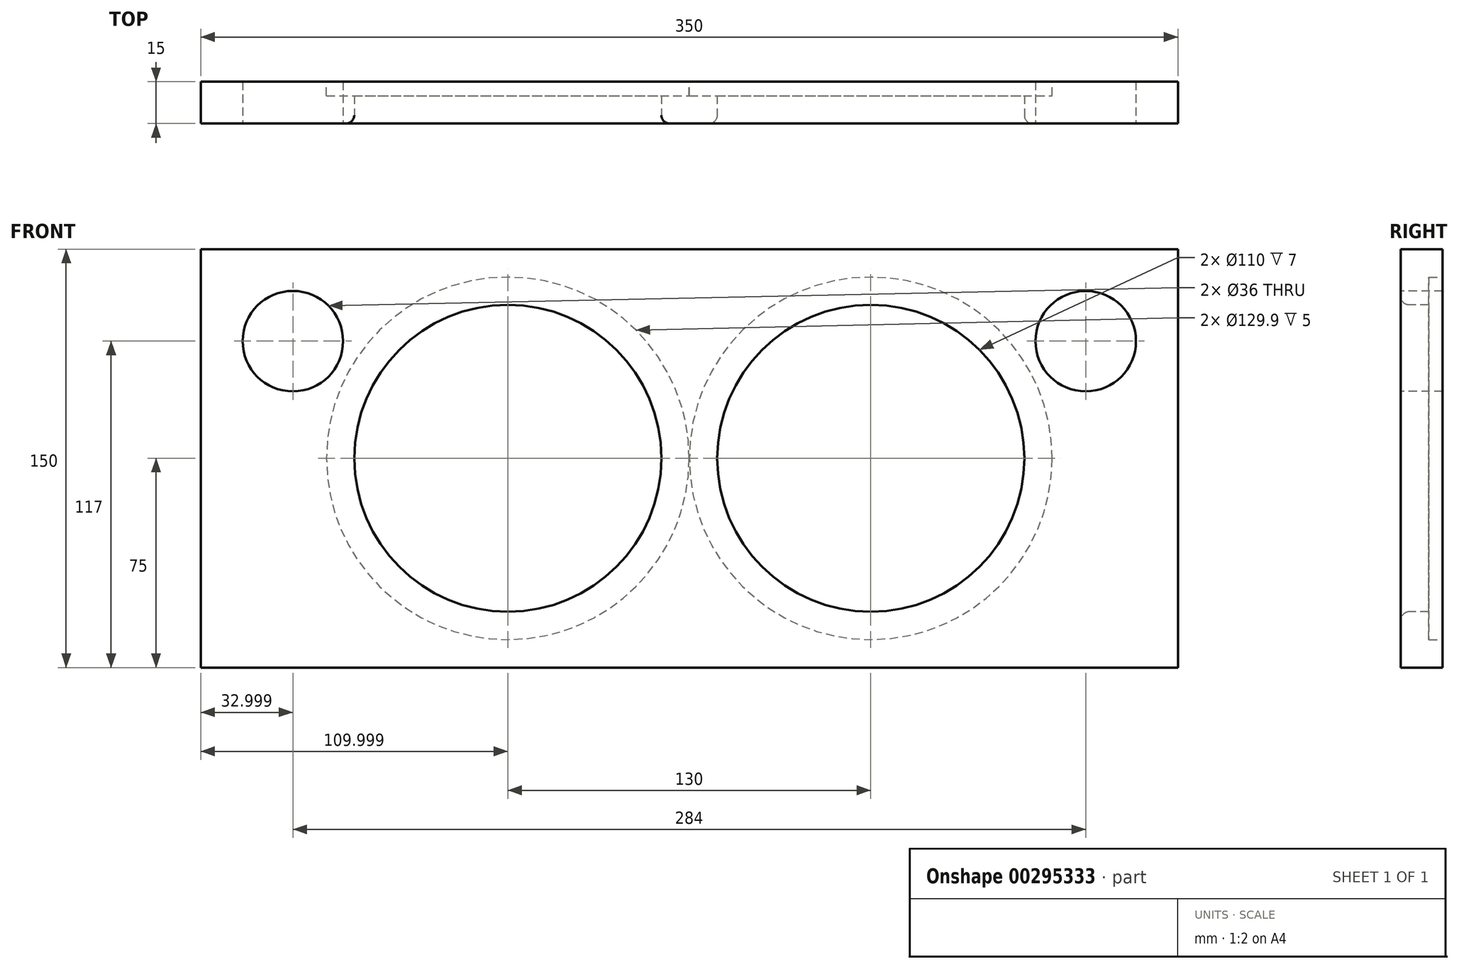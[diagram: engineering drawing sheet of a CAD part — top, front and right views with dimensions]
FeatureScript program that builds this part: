
annotation { "Feature Type Name" : "Feature", "Feature Type Description" : "" }
export const myFeature = defineFeature(function(context is Context, id is Id, definition is map)
    precondition{}
    {
        {
            var Q0;
            Q0=qCreatedBy(makeId("Front.planeOp"),FACE);
            var sketch = newSketch(context, id + "F0", { "sketchPlane" : qUnion([Q0])});
            skLineSegment(sketch, "E0.bottom", {"start": v(177.77, -75) * mm, "end": v(-172.23, -75) * mm});
            skLineSegment(sketch, "E0.top", {"start": v(177.77, 75) * mm, "end": v(-172.23, 75) * mm});
            skLineSegment(sketch, "E0.left", {"start": v(177.77, -75) * mm, "end": v(177.77, 75) * mm});
            skLineSegment(sketch, "E0.right", {"start": v(-172.23, -75) * mm, "end": v(-172.23, 75) * mm});
            skPoint(sketch, "E0.middle", {"position": v(2.77, 0) * mm});
            skLineSegment(sketch, "E1.bottom", {"start": v(67.77, 0) * mm, "end": v(-62.23, 0) * mm, "construction": true});
            skLineSegment(sketch, "E1.top", {"start": v(67.77, 0) * mm, "end": v(-62.23, 0) * mm, "construction": true});
            skLineSegment(sketch, "E1.left", {"start": v(67.77, 0) * mm, "end": v(67.77, 0) * mm});
            skLineSegment(sketch, "E1.right", {"start": v(-62.23, 0) * mm, "end": v(-62.23, 0) * mm});
            skCircle(sketch, "E2", {"center": v(-62.23, 0) * mm, "radius": 55 * mm});
            skCircle(sketch, "E3", {"center": v(67.77, 0) * mm, "radius": 55 * mm});
            skLineSegment(sketch, "E4", {"start": v(144.77, 75) * mm, "end": v(144.77, 42) * mm, "construction": true});
            skCircle(sketch, "E5", {"center": v(144.77, 42) * mm, "radius": 18 * mm});
            skLineSegment(sketch, "E6.1.0.0", {"start": v(-139.23, 75) * mm, "end": v(-139.23, 42) * mm, "construction": true});
            skCircle(sketch, "E6.1.0.1", {"center": v(-139.23, 42) * mm, "radius": 18 * mm});
            skLineSegment(sketch, "E6.direction1", {"start": v(144.77, 42) * mm, "end": v(-139.23, 42) * mm, "construction": true});
            skSolve(sketch);
        }
        {
            var Q0;
            Q0 = qSketchRegion(id + "F0", true);
            extrude(context, id + "F1", {"entities" : qUnion([Q0]), "depth" : 15 * mm, "offsetDistance" : 25 * mm});
        }
        {
            var Q0;
            Q0=makeQuery(id+"F1.opExtrude","CAP_EDGE",EDGE,{"disambiguationData":[OSD([sQuery(id+"F0.wireOp",EDGE,"E2")])],"isStart":true});
            var Q1;
            Q1=makeQuery(id+"F1.opExtrude","CAP_EDGE",EDGE,{"disambiguationData":[OSD([sQuery(id+"F0.wireOp",EDGE,"E3")])],"isStart":true});
            fillet(context, id + "F2", {"entities" : qUnion([Q0, Q1]), "radius" : 3 * mm, "tangentPropagation" : true, "defaultsChanged" : true, "vertexSettings" : [], "allowEdgeOverflow" : false});
        }
        {
            var Q0;
            Q0=makeQuery(id+"F1.opExtrude","SWEPT_BODY",BODY,{"disambiguationData":[OSD([sQuery(id+"F0.wireOp",EDGE,"E0.bottom"),sQuery(id+"F0.wireOp",EDGE,"E0.top"),sQuery(id+"F0.wireOp",EDGE,"E0.left"),sQuery(id+"F0.wireOp",EDGE,"E0.right"),sQuery(id+"F0.wireOp",EDGE,"E2"),sQuery(id+"F0.wireOp",EDGE,"E3"),sQuery(id+"F0.wireOp",EDGE,"E5"),sQuery(id+"F0.wireOp",EDGE,"E6.1.0.1")])]});
            var Q1;
            Q1=makeQuery(id+"F1.opExtrude","CAP_EDGE",EDGE,{"disambiguationData":[OSD([sQuery(id+"F0.wireOp",EDGE,"E0.right")])],"isStart":false});
            var Q2;
            Q2=makeQuery(id+"F1.opExtrude","CAP_EDGE",EDGE,{"disambiguationData":[OSD([sQuery(id+"F0.wireOp",EDGE,"E0.right")])],"isStart":false});
            transform(context, id + "F3", {"entities" : qUnion([Q0]), "transformType" : TransformType.ROTATION, "transformAxis" : qUnion([Q2]), "angle" : 180 * degree, "makeCopy" : false});
        }
        {
            var Q0;
            Q0=makeQuery(id+"F1.opExtrude","CAP_FACE",FACE,{"disambiguationData":[OSD([sQuery(id+"F0.wireOp",EDGE,"E0.bottom"),sQuery(id+"F0.wireOp",EDGE,"E0.top"),sQuery(id+"F0.wireOp",EDGE,"E0.left"),sQuery(id+"F0.wireOp",EDGE,"E0.right"),sQuery(id+"F0.wireOp",EDGE,"E2"),sQuery(id+"F0.wireOp",EDGE,"E3"),sQuery(id+"F0.wireOp",EDGE,"E5"),sQuery(id+"F0.wireOp",EDGE,"E6.1.0.1")])],"isStart":false});
            var sketch = newSketch(context, id + "F4", { "sketchPlane" : qUnion([Q0])});
            skCircle(sketch, "E7", {"center": v(282.23, 0) * mm, "radius": 55 * mm, "construction": true});
            skPoint(sketch, "E7.first.point", {"position": v(291.08, 54.28) * mm});
            skPoint(sketch, "E7.second.point", {"position": v(333.5, -19.9) * mm});
            skPoint(sketch, "E7.third.point", {"position": v(240.27, -35.56) * mm});
            skCircle(sketch, "E8", {"center": v(412.23, 0) * mm, "radius": 55 * mm, "construction": true});
            skPoint(sketch, "E8.first.point", {"position": v(416.33, 54.85) * mm});
            skPoint(sketch, "E8.second.point", {"position": v(464.7, 16.48) * mm});
            skPoint(sketch, "E8.third.point", {"position": v(369.75, -34.94) * mm});
            skCircle(sketch, "E9", {"center": v(282.23, 0) * mm, "radius": 64.95 * mm});
            skCircle(sketch, "E10", {"center": v(412.23, 0) * mm, "radius": 64.95 * mm});
            skSolve(sketch);
        }
        {
            var Q0;
            Q0 = qSketchRegion(id + "F4", true);
            extrude(context, id + "F5", {"entities" : qUnion([Q0]), "operationType" : NewBodyOperationType.REMOVE, "oppositeDirection" : true, "depth" : 5 * mm, "offsetDistance" : 25 * mm});
        }
    });
